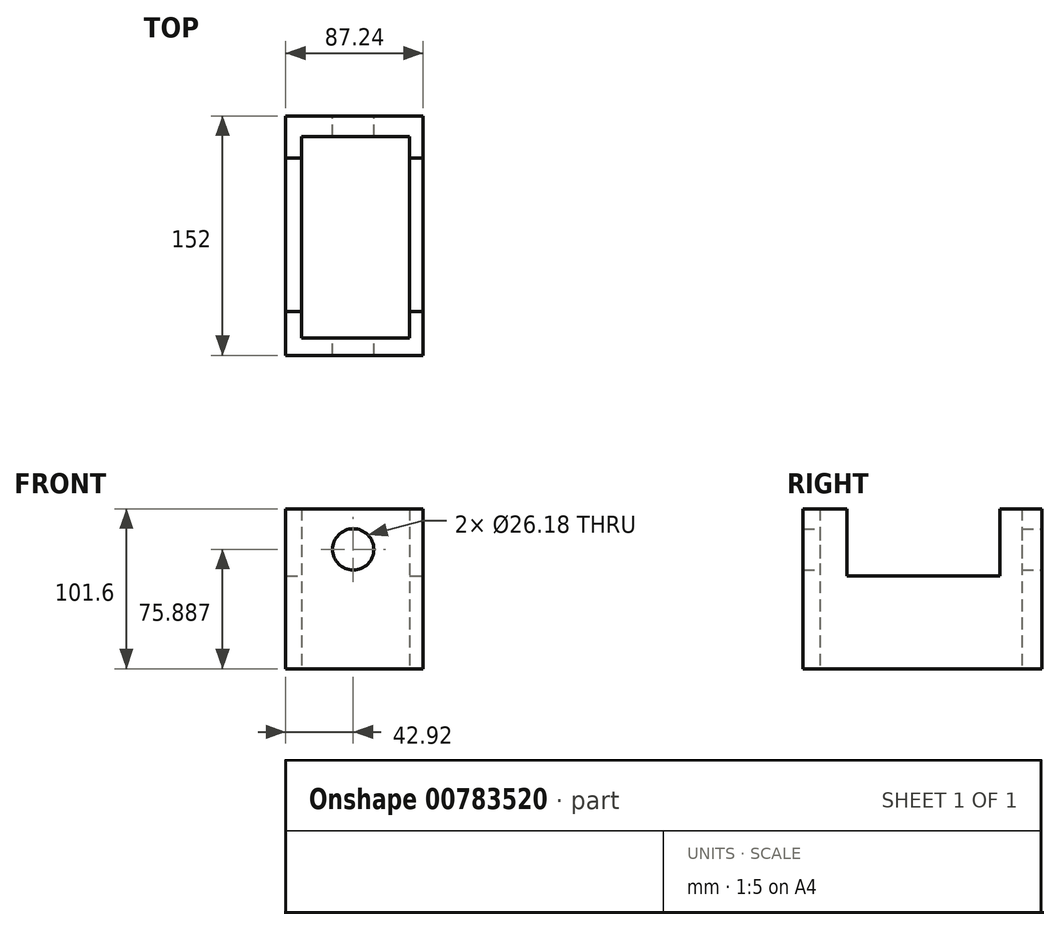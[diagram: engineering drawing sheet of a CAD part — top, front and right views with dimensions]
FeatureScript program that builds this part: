
annotation { "Feature Type Name" : "Feature", "Feature Type Description" : "" }
export const myFeature = defineFeature(function(context is Context, id is Id, definition is map)
    precondition{}
    {
        {
            var Q0;
            Q0=qCreatedBy(makeId("Top.planeOp"),FACE);
            var sketch = newSketch(context, id + "F0", { "sketchPlane" : qUnion([Q0])});
            skLineSegment(sketch, "E0.bottom", {"start": v(-42.92, 75.83) * mm, "end": v(44.32, 75.83) * mm});
            skLineSegment(sketch, "E0.top", {"start": v(-42.92, -76.17) * mm, "end": v(44.32, -76.17) * mm});
            skLineSegment(sketch, "E0.left", {"start": v(-42.92, 75.83) * mm, "end": v(-42.92, -76.17) * mm});
            skLineSegment(sketch, "E0.right", {"start": v(44.32, 75.83) * mm, "end": v(44.32, -76.17) * mm});
            skLineSegment(sketch, "E1.bottom", {"start": v(-32.8, 62.88) * mm, "end": v(35.65, 62.88) * mm});
            skLineSegment(sketch, "E1.top", {"start": v(-32.8, -65.27) * mm, "end": v(35.65, -65.27) * mm});
            skLineSegment(sketch, "E1.left", {"start": v(-32.8, 62.88) * mm, "end": v(-32.8, -65.27) * mm});
            skLineSegment(sketch, "E1.right", {"start": v(35.65, 62.88) * mm, "end": v(35.65, -65.27) * mm});
            skSolve(sketch);
        }
        {
            var Q0;
            Q0=makeQuery(id+"F0.imprint","IMPRINT",FACE,{"disambiguationData":[TD([[makeQuery(id+"F0.imprint","IMPRINT",EDGE,{"derivedFrom":sQuery(id+"F0.wireOp",EDGE,"E0.bottom")}),-1.0]])]});
            extrude(context, id + "F1", {"entities" : qUnion([Q0]), "depth" : 101.6 * mm, "offsetDistance" : 25.4 * mm});
        }
        {
            var Q0;
            Q0=makeQuery(id+"F1.opExtrude","SWEPT_FACE",FACE,{"disambiguationData":[OSD([sQuery(id+"F0.wireOp",EDGE,"E0.right")])]});
            var sketch = newSketch(context, id + "F2", { "sketchPlane" : qUnion([Q0])});
            skLineSegment(sketch, "E2.bottom", {"start": v(-48.22, 101.6) * mm, "end": v(49.2, 101.6) * mm});
            skLineSegment(sketch, "E2.top", {"start": v(-48.22, 59.13) * mm, "end": v(49.2, 59.13) * mm});
            skLineSegment(sketch, "E2.left", {"start": v(-48.22, 101.6) * mm, "end": v(-48.22, 59.13) * mm});
            skLineSegment(sketch, "E2.right", {"start": v(49.2, 101.6) * mm, "end": v(49.2, 59.13) * mm});
            skSolve(sketch);
        }
        {
            var Q0;
            Q0=makeQuery(id+"F2.imprint","IMPRINT",FACE,{"disambiguationData":[TD([[makeQuery(id+"F2.imprint","IMPRINT",EDGE,{"derivedFrom":sQuery(id+"F2.wireOp",EDGE,"E2.bottom")}),1.0]])]});
            extrude(context, id + "F3", {"entities" : qUnion([Q0]), "operationType" : NewBodyOperationType.REMOVE, "oppositeDirection" : true, "depth" : 105.4 * mm, "offsetDistance" : 25.4 * mm});
        }
        {
            var Q0;
            Q0=makeQuery(id+"F1.opExtrude","SWEPT_FACE",FACE,{"disambiguationData":[OSD([sQuery(id+"F0.wireOp",EDGE,"E0.bottom")])]});
            var sketch = newSketch(context, id + "F4", { "sketchPlane" : qUnion([Q0])});
            skCircle(sketch, "E3", {"center": v(0, 75.89) * mm, "radius": 13.09 * mm});
            skSolve(sketch);
        }
        {
            var Q0;
            Q0=makeQuery(id+"F4.imprint","IMPRINT",FACE,{"disambiguationData":[TD([[makeQuery(id+"F4.imprint","IMPRINT",EDGE,{"derivedFrom":sQuery(id+"F4.wireOp",EDGE,"E3")}),1.0]])]});
            extrude(context, id + "F5", {"entities" : qUnion([Q0]), "operationType" : NewBodyOperationType.REMOVE, "oppositeDirection" : true, "depth" : 209.3 * mm, "offsetDistance" : 25.4 * mm});
        }
    });
